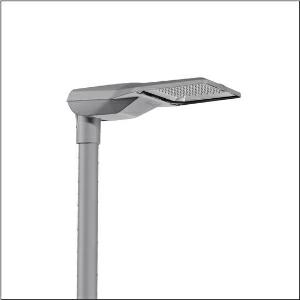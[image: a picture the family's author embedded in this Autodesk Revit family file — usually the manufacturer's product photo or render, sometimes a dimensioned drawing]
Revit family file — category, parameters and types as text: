
# Revit family: streetlight_sl_21_iq_midi___st1_5a_5xe3p31d08mb_51c0
name_source: partatom
category: Lighting Fixtures
units: mm (PartAtom-declared; Revit-internal decimal feet)

## family parameters
Cut with Voids When Loaded = No
Host = Face
Light Source = No
Part Type = Normal
Room Calculation Point = No
Round Connector Dimension = Use Diameter
Shared = No

## types (1)
- --- (1 x LED, 19170 lm, 146.7 W, 3000K)
    Apparent Load = 147 VA
    CIE Flux Codes = 22 53 95 100 100
    Color Rendering = 70
    Color Temperature = 3000K
    Default Elevation = 1800 mm
    Description = Streetlight SL 21 iQ midi, mast luminaire, primary light control with lens, of PMMA, primary optical cover: cover, of toughened safety glass, transparent, light distribution: ST1.5a, light emission: direct distribution, primary light characteristic: asymmetric, installation type: post-top, side-entry, LED, High Power LED, rated luminous flux: 19.170lm, luminous efficacy: 131lm/W, light colour: 730, colour temperature: 3000K, control: Auto-Match, Temp-Guard, Lumen-Switch, Night-Set, Smart-Wire, Light-Fading, Desk-Remote (wireless, voltage-free reading and setting of iQ features in the workshop via application-optimized NFC function/RFID function), optimised constant luminous flux control (CLO 2.0), presetting dimming linear, mains connection: 230..240V, AC, 50/60Hz, start of lifetime: 147W, end of service life: 161W, reduction: 62W, luminaire housing, of diecast aluminium, powder-coated, Siteco® metallic grey (DB 702S), corrosivity category C5 mid according to DIN EN ISO 12944, please order mast flange separately, inclination adjustable: 0°, 5°, 10°, 15°, sealing non-destructively replaceable, multi-level sealing system, length: 644mm, width: 335mm, height: 110mm, mast flange for spigot size: 42mm (side-entry): 5XC10008XM4, 60/48mm (side-entry/post-top): 5XC10108XM2, 76/60mm (side-entry/post-top): 5XC10108XM1, protection rating (complete): IP66, insulation class (complete): insulation class II (safety insulation), certification: CE, ENEC, ENEC+, VDE, impact resistance: IK09, permissible operating ambient temperature for outdoor applications: -40..+50°C, standard-compliant lighting for roads and squares, packaging unit: 1 piece

Light Distribution: ST1.5a
    Height = 111 mm
    Lamp = 1 x LED
    Lamp Light Flux = 19170 lm
    Lamp Power = 146.7 W
    Lamp count = 1
    Length = 644 mm
    Luminous efficacy = 131 lm/W
    Manufacturer = Siteco
    ModVariant = No
    Model = 5XE3P31D08MB
    Number of Poles = 1
    OnlyDefault = Yes
    Power Factor = 1
    Product Name = Streetlight SL 21 iQ midi | ST1.5a
    Product group = mast luminaire | pylon top
    ProductGroupID = 6100
    Protection Class = Protection class II
    Protection Degree = IP 66
    RLX_Detail_Level = 1
    RLX_Emergency_Light_Flux = 0 lm
    RLX_Emergency_Type = 0
    RLX_Emergency_Type_DB = No
    RlxData = <blob elided: 94525 chars, md5=a03961b5>
    Socket = socket
    Standby Power = 0 W
    System Light Flux = 19169 lm
    System Power = 147 W
    Type Comments = factory setting: luminous flux: 100 % | dim-lin: 254 | 753 mA
    Type Image = l_1004298.jpg
    URL = http://relux.com
    VarID = @adj_109699
    Voltage = 0 V
    Weight = 0.00 kg
    Width = 336 mm

## geometry (parser evidence)
native form markers: Blend x4, Sweep x9
no freeform markers — native parametric forms only
